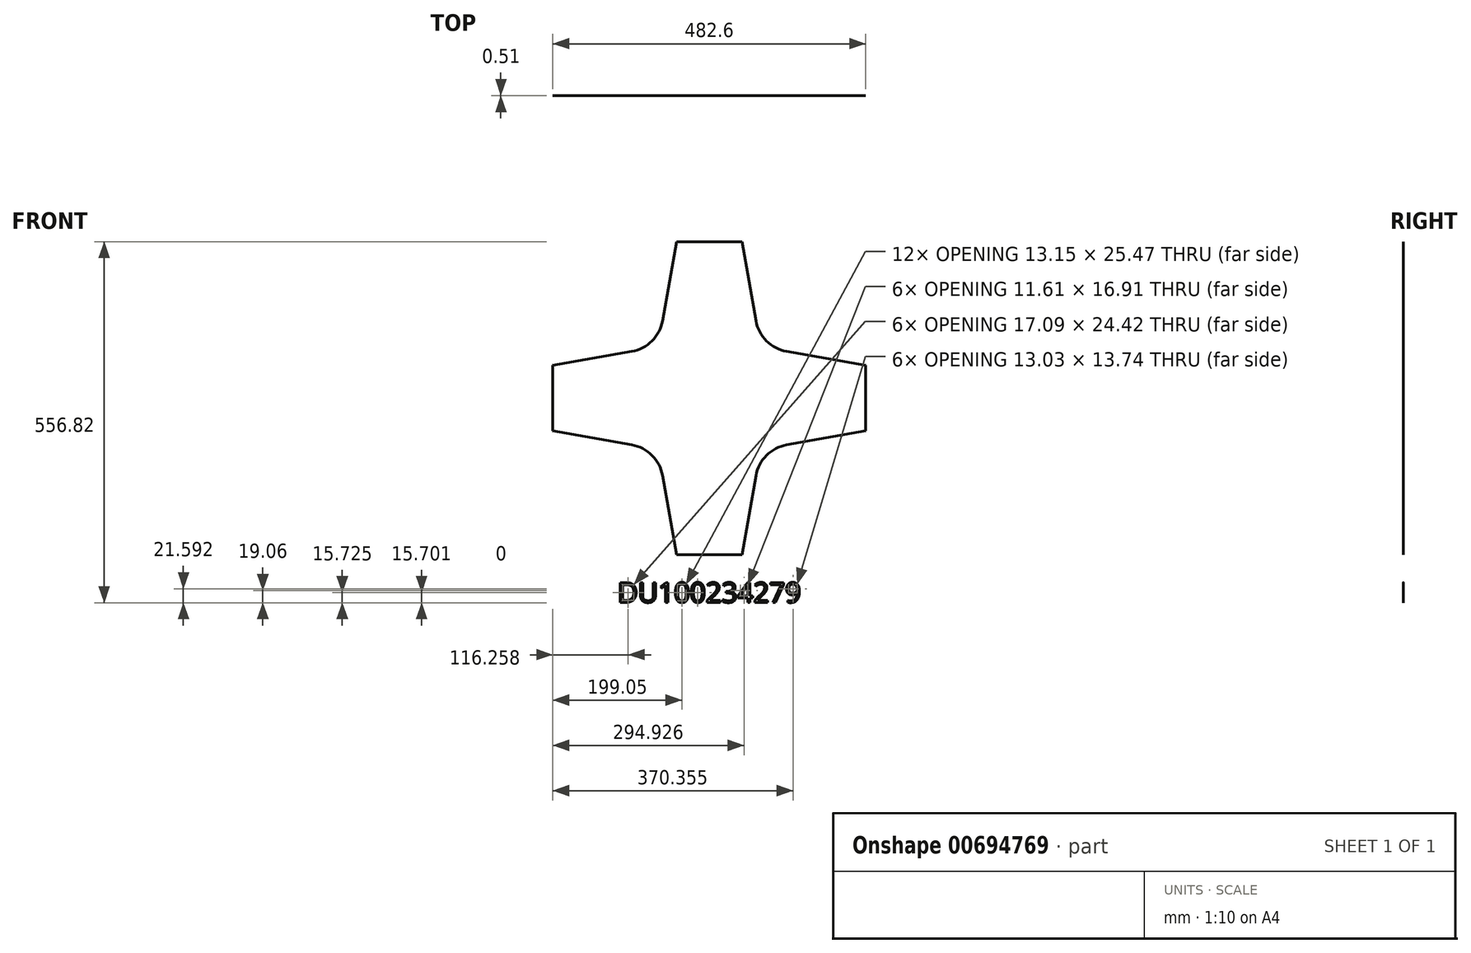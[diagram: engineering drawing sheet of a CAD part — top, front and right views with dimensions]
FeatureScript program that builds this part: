
annotation { "Feature Type Name" : "Feature", "Feature Type Description" : "" }
export const myFeature = defineFeature(function(context is Context, id is Id, definition is map)
    precondition{}
    {
        {
            var Q0;
            Q0=qCreatedBy(makeId("Front.planeOp"),FACE);
            var sketch = newSketch(context, id + "F0", { "sketchPlane" : qUnion([Q0])});
            skLineSegment(sketch, "E0", {"start": v(0, 0) * mm, "end": v(0, 264.46) * mm});
            skPoint(sketch, "E1", {"position": v(-129.54, 129.54) * mm});
            skArc(sketch, "E2", {"start": v(-119.4, 72) * mm, "mid": v(-88.23, 88.23) * mm, "end": v(-72, 119.4) * mm});
            skPoint(sketch, "E3", {"position": v(0, 241.3) * mm});
            skLineSegment(sketch, "E4", {"start": v(-79.11, 79.11) * mm, "end": v(-50.51, 241.3) * mm});
            skLineSegment(sketch, "E5", {"start": v(0, 241.3) * mm, "end": v(-50.51, 241.3) * mm});
            skPoint(sketch, "E6.MirrorCS.end.orphan", {"position": v(50.51, 241.3) * mm});
            skLineSegment(sketch, "E7", {"start": v(-79.11, 79.11) * mm, "end": v(-241.3, 50.51) * mm});
            skPoint(sketch, "E8", {"position": v(-241.3, 0) * mm});
            skLineSegment(sketch, "E9", {"start": v(-241.3, 0) * mm, "end": v(-241.3, 50.51) * mm});
            skLineSegment(sketch, "E10.MirrorCS", {"start": v(0, 241.3) * mm, "end": v(50.51, 241.3) * mm});
            skLineSegment(sketch, "E11.MirrorCS", {"start": v(72, 119.4) * mm, "end": v(50.51, 241.3) * mm});
            skArc(sketch, "E12.MirrorCS", {"start": v(119.4, 72) * mm, "mid": v(88.23, 88.23) * mm, "end": v(72, 119.4) * mm});
            skLineSegment(sketch, "E13.MirrorCS", {"start": v(119.4, 72) * mm, "end": v(241.3, 50.51) * mm});
            skLineSegment(sketch, "E14.MirrorCS", {"start": v(241.3, 0) * mm, "end": v(241.3, 50.51) * mm});
            skLineSegment(sketch, "E15.MirrorCS", {"start": v(241.3, 0) * mm, "end": v(241.3, -50.51) * mm});
            skLineSegment(sketch, "E16.MirrorCS", {"start": v(119.4, -72) * mm, "end": v(241.3, -50.51) * mm});
            skArc(sketch, "E17.MirrorCS", {"start": v(119.4, -72) * mm, "mid": v(88.23, -88.23) * mm, "end": v(72, -119.4) * mm});
            skLineSegment(sketch, "E18.MirrorCS", {"start": v(72, -119.4) * mm, "end": v(50.51, -241.3) * mm});
            skLineSegment(sketch, "E19.MirrorCS", {"start": v(0, -241.3) * mm, "end": v(50.51, -241.3) * mm});
            skLineSegment(sketch, "E20.MirrorCS", {"start": v(0, -241.3) * mm, "end": v(-50.51, -241.3) * mm});
            skLineSegment(sketch, "E21.MirrorCS", {"start": v(-72, -119.4) * mm, "end": v(-50.51, -241.3) * mm});
            skArc(sketch, "E22.MirrorCS", {"start": v(-119.4, -72) * mm, "mid": v(-88.23, -88.23) * mm, "end": v(-72, -119.4) * mm});
            skLineSegment(sketch, "E23.MirrorCS", {"start": v(-119.4, -72) * mm, "end": v(-241.3, -50.51) * mm});
            skLineSegment(sketch, "E24.MirrorCS", {"start": v(-241.3, 0) * mm, "end": v(-241.3, -50.51) * mm});
            skPoint(sketch, "E25.startSnap0", {"position": v(-88.23, 88.23) * mm});
            skPoint(sketch, "E25.start.orphan", {"position": v(-51.39, 88.23) * mm});
            skLineSegment(sketch, "E26.MirrorCS", {"start": v(79.11, 79.11) * mm, "end": v(50.51, 241.3) * mm});
            skLineSegment(sketch, "E27.MirrorCS", {"start": v(79.11, 79.11) * mm, "end": v(241.3, 50.51) * mm});
            skLineSegment(sketch, "E28.MirrorCS", {"start": v(79.11, -79.11) * mm, "end": v(50.51, -241.3) * mm});
            skLineSegment(sketch, "E29.MirrorCS", {"start": v(79.11, -79.11) * mm, "end": v(241.3, -50.51) * mm});
            skLineSegment(sketch, "E30.MirrorCS", {"start": v(-79.11, -79.11) * mm, "end": v(-50.51, -241.3) * mm});
            skLineSegment(sketch, "E31.MirrorCS", {"start": v(-79.11, -79.11) * mm, "end": v(-241.3, -50.51) * mm});
            skText(sketch, "E32", { "text": "DU100234279", "fontName": "OpenSans-Regular.ttf"});
            const initialGuessF0  = {"E32": [-0.14134, -0.3151, 1, 0, 0.03083]};
            skSetInitialGuess(sketch, initialGuessF0);
            skSolve(sketch);
        }
        {
            var Q0;
            Q0 = qSketchRegion(id + "F0", true);
            extrude(context, id + "F1", {"entities" : qUnion([Q0]), "depth" : 0.5 * mm, "offsetDistance" : 25.4 * mm});
        }
    });
